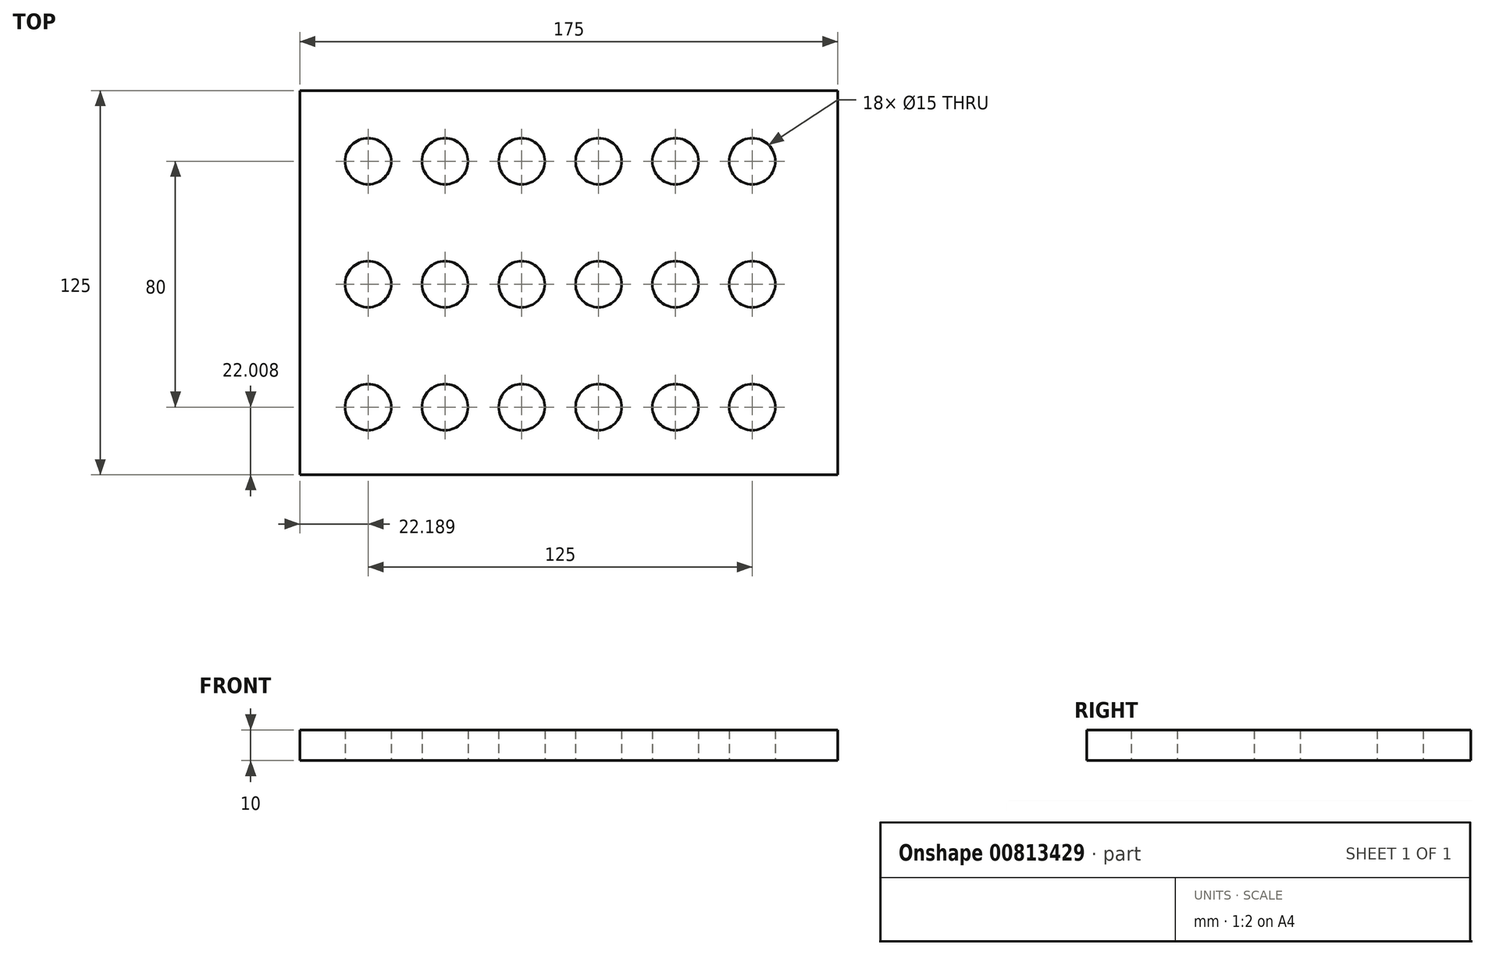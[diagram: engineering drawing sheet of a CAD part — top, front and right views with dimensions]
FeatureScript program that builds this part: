
annotation { "Feature Type Name" : "Feature", "Feature Type Description" : "" }
export const myFeature = defineFeature(function(context is Context, id is Id, definition is map)
    precondition{}
    {
        {
            var Q0;
            Q0=qCreatedBy(makeId("Top.planeOp"),FACE);
            var sketch = newSketch(context, id + "F0", { "sketchPlane" : qUnion([Q0])});
            skLineSegment(sketch, "E0.bottom", {"start": v(-87.5, 62.5) * mm, "end": v(87.5, 62.5) * mm});
            skLineSegment(sketch, "E0.top", {"start": v(-87.5, -62.5) * mm, "end": v(87.5, -62.5) * mm});
            skLineSegment(sketch, "E0.left", {"start": v(-87.5, 62.5) * mm, "end": v(-87.5, -62.5) * mm});
            skLineSegment(sketch, "E0.right", {"start": v(87.5, 62.5) * mm, "end": v(87.5, -62.5) * mm});
            skLineSegment(sketch, "E1", {"start": v(-87.5, 62.5) * mm, "end": v(87.5, -62.5) * mm, "construction": true});
            skLineSegment(sketch, "E2", {"start": v(-87.5, -62.5) * mm, "end": v(87.5, 62.5) * mm, "construction": true});
            skCircle(sketch, "E3", {"center": v(-65.31, 39.5) * mm, "radius": 7.5 * mm});
            skCircle(sketch, "E4.0.1.0", {"center": v(-65.31, -0.5) * mm, "radius": 7.5 * mm});
            skCircle(sketch, "E4.0.2.0", {"center": v(-65.31, -40.5) * mm, "radius": 7.5 * mm});
            skCircle(sketch, "E4.1.0.0", {"center": v(-40.31, 39.5) * mm, "radius": 7.5 * mm});
            skCircle(sketch, "E4.1.1.0", {"center": v(-40.31, -0.5) * mm, "radius": 7.5 * mm});
            skCircle(sketch, "E4.1.2.0", {"center": v(-40.31, -40.5) * mm, "radius": 7.5 * mm});
            skCircle(sketch, "E4.2.0.0", {"center": v(-15.31, 39.5) * mm, "radius": 7.5 * mm});
            skCircle(sketch, "E4.2.1.0", {"center": v(-15.31, -0.5) * mm, "radius": 7.5 * mm});
            skCircle(sketch, "E4.2.2.0", {"center": v(-15.31, -40.5) * mm, "radius": 7.5 * mm});
            skCircle(sketch, "E4.3.0.0", {"center": v(9.69, 39.5) * mm, "radius": 7.5 * mm});
            skCircle(sketch, "E4.3.1.0", {"center": v(9.69, -0.5) * mm, "radius": 7.5 * mm});
            skCircle(sketch, "E4.3.2.0", {"center": v(9.69, -40.5) * mm, "radius": 7.5 * mm});
            skCircle(sketch, "E4.4.0.0", {"center": v(34.69, 39.5) * mm, "radius": 7.5 * mm});
            skCircle(sketch, "E4.4.1.0", {"center": v(34.69, -0.5) * mm, "radius": 7.5 * mm});
            skCircle(sketch, "E4.4.2.0", {"center": v(34.69, -40.5) * mm, "radius": 7.5 * mm});
            skCircle(sketch, "E4.5.0.0", {"center": v(59.69, 39.5) * mm, "radius": 7.5 * mm});
            skCircle(sketch, "E4.5.1.0", {"center": v(59.69, -0.5) * mm, "radius": 7.5 * mm});
            skCircle(sketch, "E4.5.2.0", {"center": v(59.69, -40.5) * mm, "radius": 7.5 * mm});
            skLineSegment(sketch, "E4.direction1", {"start": v(-65.31, 39.5) * mm, "end": v(-40.31, 39.5) * mm, "construction": true});
            skLineSegment(sketch, "E4.direction2", {"start": v(-65.31, 39.5) * mm, "end": v(-65.31, -0.5) * mm, "construction": true});
            skSolve(sketch);
        }
        {
            var Q0;
            Q0 = qSketchRegion(id + "F0", true);
            extrude(context, id + "F1", {"entities" : qUnion([Q0]), "depth" : 10 * mm, "offsetDistance" : 25.4 * mm});
        }
    });
